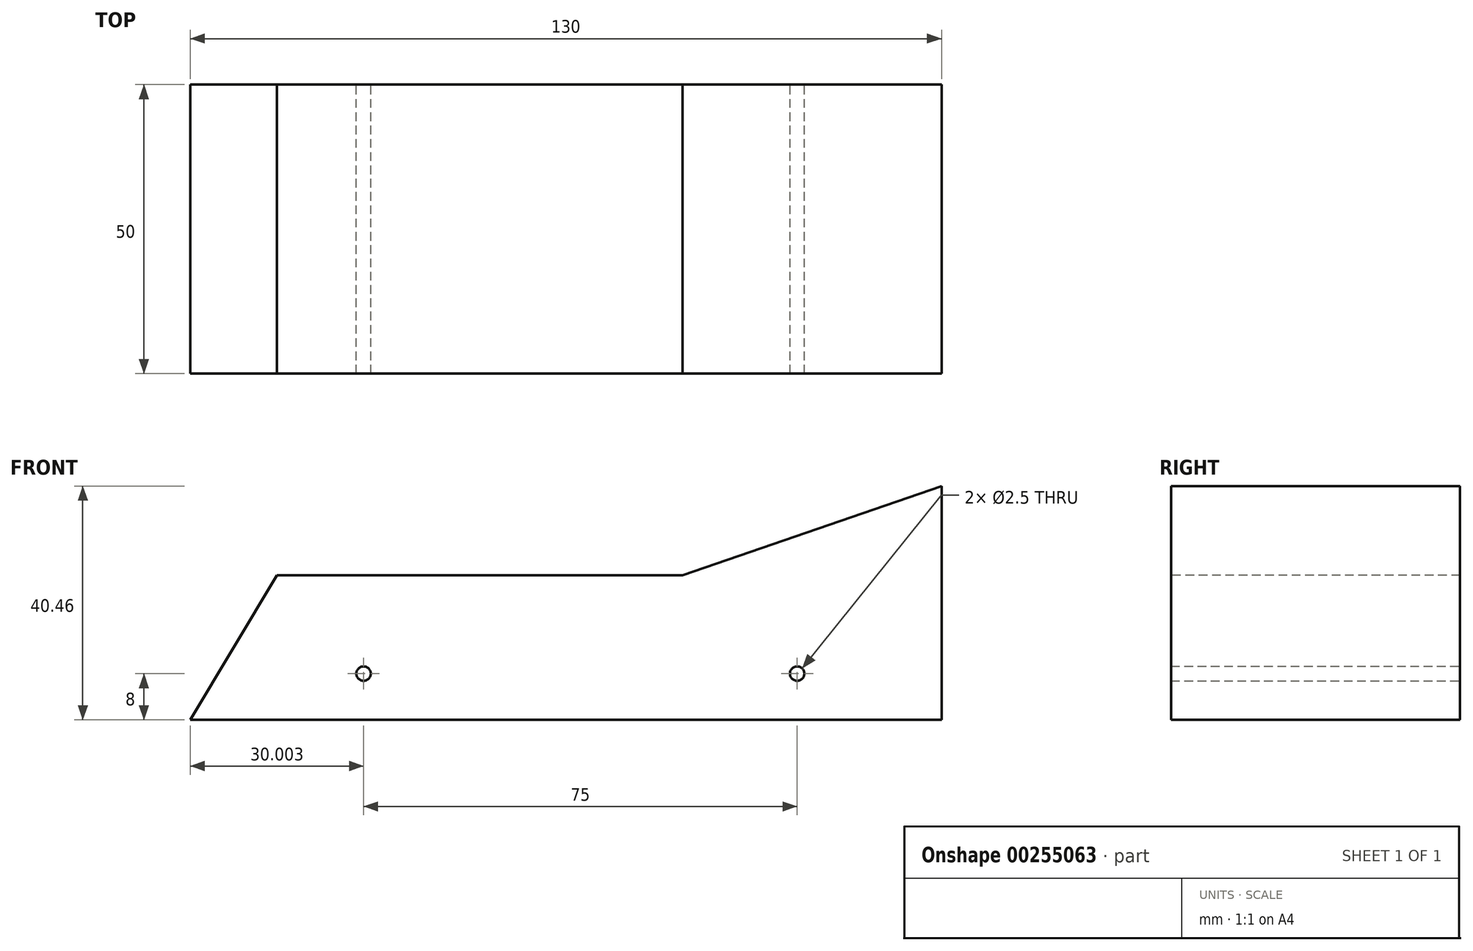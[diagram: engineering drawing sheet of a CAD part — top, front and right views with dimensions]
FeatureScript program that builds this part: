
annotation { "Feature Type Name" : "Feature", "Feature Type Description" : "" }
export const myFeature = defineFeature(function(context is Context, id is Id, definition is map)
    precondition{}
    {
        {
            var Q0;
            Q0=qCreatedBy(makeId("Front.planeOp"),FACE);
            var sketch = newSketch(context, id + "F0", { "sketchPlane" : qUnion([Q0])});
            skLineSegment(sketch, "E0.bottom", {"start": v(52.3, 25) * mm, "end": v(-47.7, 25) * mm});
            skLineSegment(sketch, "E0.top", {"start": v(52.3, -25) * mm, "end": v(-47.7, -25) * mm});
            skLineSegment(sketch, "E0.left", {"start": v(52.3, 25) * mm, "end": v(52.3, -25) * mm});
            skPoint(sketch, "E0.middle", {"position": v(2.3, 0) * mm});
            skLineSegment(sketch, "E1", {"start": v(-47.7, -25) * mm, "end": v(-77.7, -25) * mm});
            skLineSegment(sketch, "E2", {"start": v(-77.7, -25) * mm, "end": v(-47.7, 25) * mm});
            skLineSegment(sketch, "E3", {"start": v(52.3, -25) * mm, "end": v(27.3, -25) * mm});
            skLineSegment(sketch, "E4", {"start": v(27.3, -18.25) * mm, "end": v(27.3, -17) * mm});
            skLineSegment(sketch, "E5", {"start": v(-47.7, -18.25) * mm, "end": v(-47.7, -17) * mm});
            skCircle(sketch, "E6", {"center": v(-47.7, -17) * mm, "radius": 1.25 * mm});
            skCircle(sketch, "E7", {"center": v(27.3, -17) * mm, "radius": 1.25 * mm});
            skSolve(sketch);
        }
        {
            var Q0;
            Q0=makeQuery(id+"F0.imprint","IMPRINT",FACE,{"disambiguationData":[TD([[makeQuery(id+"F0.imprint","IMPRINT",EDGE,{"derivedFrom":sQuery(id+"F0.wireOp",EDGE,"E0.bottom")}),1.0]])]});
            extrude(context, id + "F1", {"entities" : qUnion([Q0]), "depth" : 50 * mm});
        }
        {
            var Q0;
            Q0=makeQuery(id+"F1.opExtrude","CAP_FACE",FACE,{"disambiguationData":[OSD([sQuery(id+"F0.wireOp",EDGE,"E0.bottom"),sQuery(id+"F0.wireOp",EDGE,"E0.top"),sQuery(id+"F0.wireOp",EDGE,"E0.left"),sQuery(id+"F0.wireOp",EDGE,"E1"),sQuery(id+"F0.wireOp",EDGE,"E2"),sQuery(id+"F0.wireOp",EDGE,"E3"),sQuery(id+"F0.wireOp",EDGE,"E6"),sQuery(id+"F0.wireOp",EDGE,"E7")])],"isStart":false});
            var sketch = newSketch(context, id + "F2", { "sketchPlane" : qUnion([Q0])});
            skLineSegment(sketch, "E8", {"start": v(-62.7, 0) * mm, "end": v(-28.94, 0) * mm});
            skPoint(sketch, "E8.endSnap0", {"position": v(-62.7, 0) * mm});
            skLineSegment(sketch, "E9", {"start": v(-28.94, 0) * mm, "end": v(7.45, 0) * mm});
            skLineSegment(sketch, "E10", {"start": v(7.45, 0) * mm, "end": v(52.3, 15.46) * mm});
            skSolve(sketch);
        }
        {
            var Q0;
            {var subQ3=sQuery(id+"F2.wireOp",EDGE,"E8");Q0=makeQuery(id+"F2.imprint","IMPRINT",FACE,{"disambiguationData":[TD([[makeQuery(id+"F2.imprint","IMPRINT",EDGE,{"derivedFrom":subQ3}),1.0]])]});}
            extrude(context, id + "F3", {"entities" : qUnion([Q0]), "operationType" : NewBodyOperationType.REMOVE, "endBound" : BoundingType.THROUGH_ALL, "oppositeDirection" : true, "depth" : 50 * mm});
        }
    });
